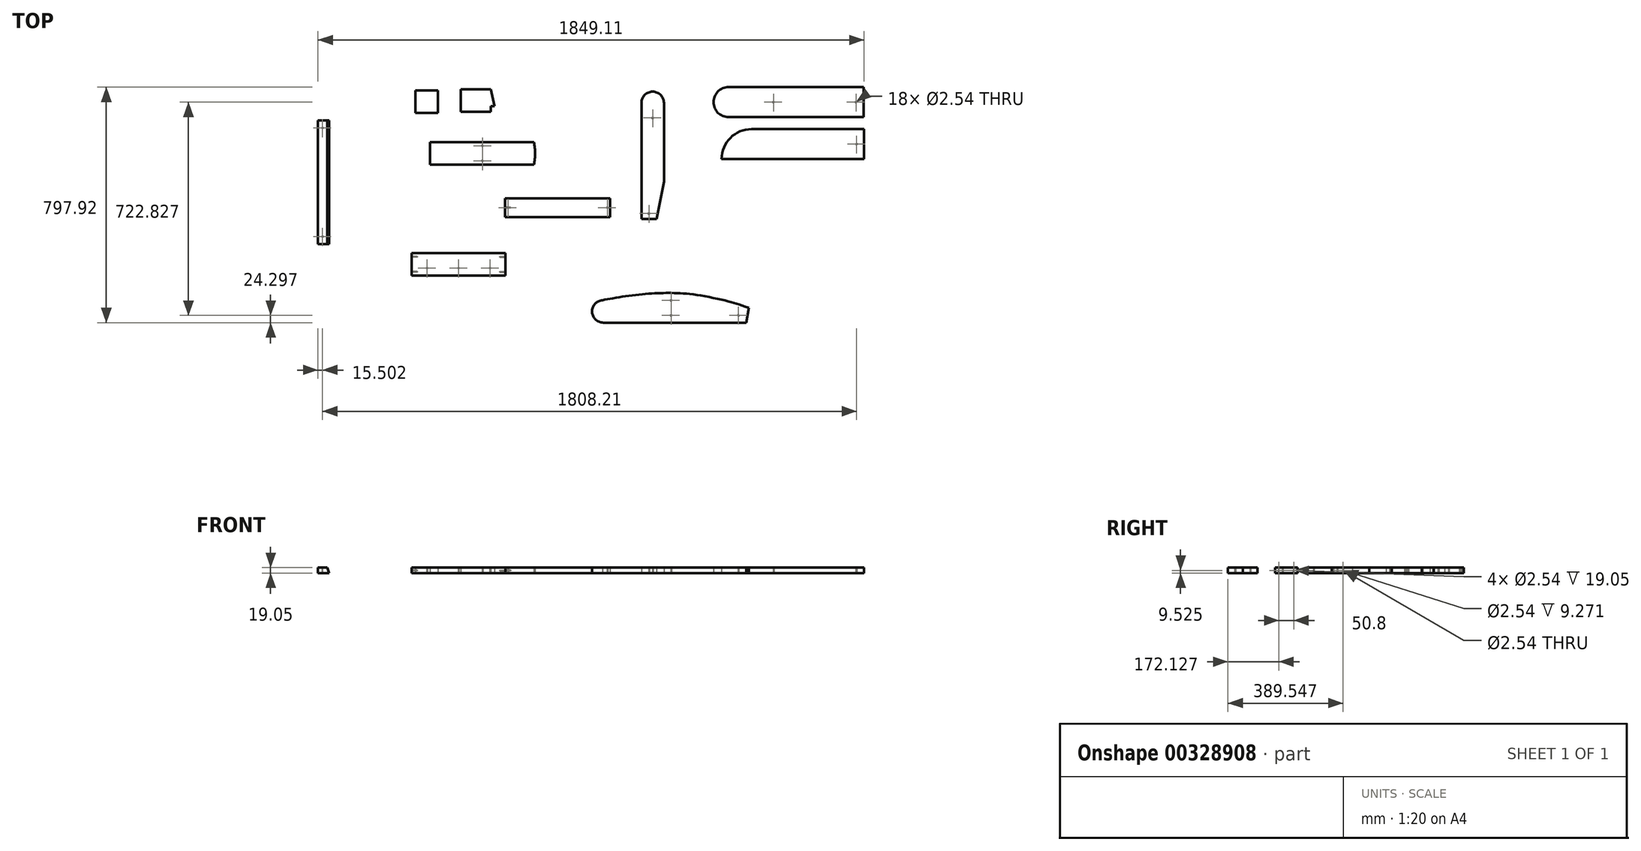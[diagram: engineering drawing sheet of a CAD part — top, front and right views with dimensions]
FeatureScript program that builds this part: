
annotation { "Feature Type Name" : "Feature", "Feature Type Description" : "" }
export const myFeature = defineFeature(function(context is Context, id is Id, definition is map)
    precondition{}
    {
        {
            var Q0;
            Q0=qCreatedBy(makeId("Top.planeOp"),FACE);
            var sketch = newSketch(context, id + "F0", { "sketchPlane" : qUnion([Q0])});
            skLineSegment(sketch, "E0", {"start": v(-60.93, -334.39) * mm, "end": v(-10.13, -334.39) * mm});
            skLineSegment(sketch, "E1", {"start": v(-10.13, -334.39) * mm, "end": v(15.27, -207.39) * mm});
            skLineSegment(sketch, "E2", {"start": v(15.27, -207.39) * mm, "end": v(15.27, 59.31) * mm});
            skLineSegment(sketch, "E3", {"start": v(-60.93, -334.39) * mm, "end": v(-60.93, 59.31) * mm});
            skLineSegment(sketch, "E4", {"start": v(-22.83, 97.41) * mm, "end": v(-22.83, 97.41) * mm});
            skPoint(sketch, "E5.visualSharp", {"position": v(-60.93, 97.41) * mm});
            skArc(sketch, "E5.filletArc", {"start": v(-22.83, 97.41) * mm, "mid": v(-49.77, 86.25) * mm, "end": v(-60.93, 59.31) * mm});
            skPoint(sketch, "E6.visualSharp", {"position": v(15.27, 97.41) * mm});
            skArc(sketch, "E6.filletArc", {"start": v(15.27, 59.31) * mm, "mid": v(4.1, 86.25) * mm, "end": v(-22.83, 97.41) * mm});
            skCircle(sketch, "E7", {"center": v(-35.53, -315.34) * mm, "radius": 1.27 * mm});
            skLineSegment(sketch, "E8", {"start": v(-22.83, 59.31) * mm, "end": v(-22.83, 8.51) * mm});
            skCircle(sketch, "E9", {"center": v(-22.83, 8.51) * mm, "radius": 1.27 * mm});
            skSolve(sketch);
        }
        {
            var Q0;
            Q0=makeQuery(id+"F0.imprint","IMPRINT",FACE,{"disambiguationData":[TD([[makeQuery(id+"F0.imprint","IMPRINT",EDGE,{"derivedFrom":sQuery(id+"F0.wireOp",EDGE,"E0")}),1.0]])]});
            extrude(context, id + "F1", {"entities" : qUnion([Q0]), "depth" : 19.05 * mm});
        }
        {
            var Q0;
            Q0=makeQuery(id+"F1.opExtrude","SWEPT_BODY",BODY,{"disambiguationData":[OSD([sQuery(id+"F0.wireOp",EDGE,"E0"),sQuery(id+"F0.wireOp",EDGE,"E1"),sQuery(id+"F0.wireOp",EDGE,"E2"),sQuery(id+"F0.wireOp",EDGE,"E3"),sQuery(id+"F0.wireOp",EDGE,"E5.filletArc"),sQuery(id+"F0.wireOp",EDGE,"E6.filletArc")])]});
            transform(context, id + "F2", {"entities" : qUnion([Q0]), "transformType" : TransformType.TRANSLATION_3D, "dx" : 812.8 * mm, "dy" : 0 * mm, "dz" : 0 * mm, "makeCopy" : true});
        }
        {
            var Q0;
            Q0=makeQuery(id+"F2.opPattern","COPY",BODY,{"derivedFrom":makeQuery(id+"F1.opExtrude","SWEPT_BODY",BODY,{"disambiguationData":[OSD([sQuery(id+"F0.wireOp",EDGE,"E0"),sQuery(id+"F0.wireOp",EDGE,"E1"),sQuery(id+"F0.wireOp",EDGE,"E2"),sQuery(id+"F0.wireOp",EDGE,"E3"),sQuery(id+"F0.wireOp",EDGE,"E5.filletArc"),sQuery(id+"F0.wireOp",EDGE,"E6.filletArc")])]}),"instanceName":"1"});
            deleteBodies(context, id + "F3", {"entities" : qUnion([Q0])});
        }
        {
            var Q0;
            Q0=qCreatedBy(makeId("Top.planeOp"),FACE);
            var sketch = newSketch(context, id + "F4", { "sketchPlane" : qUnion([Q0])});
            skLineSegment(sketch, "E10", {"start": v(693.1, -131) * mm, "end": v(210.5, -131) * mm});
            skLineSegment(sketch, "E11", {"start": v(210.5, -131) * mm, "end": v(210.5, -131) * mm});
            skLineSegment(sketch, "E12", {"start": v(312.1, -29.4) * mm, "end": v(693.1, -29.4) * mm});
            skLineSegment(sketch, "E13", {"start": v(693.1, -29.4) * mm, "end": v(693.1, -131) * mm});
            skPoint(sketch, "E14.visualSharp", {"position": v(210.5, -29.4) * mm});
            skArc(sketch, "E14.filletArc", {"start": v(312.1, -29.4) * mm, "mid": v(240.26, -59.17) * mm, "end": v(210.5, -131) * mm});
            skLineSegment(sketch, "E15", {"start": v(693.1, -80.2) * mm, "end": v(667.7, -80.2) * mm});
            skCircle(sketch, "E16", {"center": v(667.7, -80.2) * mm, "radius": 1.27 * mm});
            skSolve(sketch);
        }
        {
            var Q0;
            Q0=makeQuery(id+"F4.imprint","IMPRINT",FACE,{"disambiguationData":[TD([[makeQuery(id+"F4.imprint","IMPRINT",EDGE,{"derivedFrom":sQuery(id+"F4.wireOp",EDGE,"E10")}),-1.0]])]});
            extrude(context, id + "F5", {"entities" : qUnion([Q0]), "depth" : 19.05 * mm});
        }
        {
            var Q0;
            Q0=qCreatedBy(makeId("Top.planeOp"),FACE);
            var sketch = newSketch(context, id + "F6", { "sketchPlane" : qUnion([Q0])});
            skLineSegment(sketch, "E17", {"start": v(691.12, 11.16) * mm, "end": v(691.12, 112.76) * mm});
            skPoint(sketch, "E18.visualSharp", {"position": v(183.12, 112.76) * mm});
            skLineSegment(sketch, "E19", {"start": v(691.12, 61.96) * mm, "end": v(665.72, 61.96) * mm});
            skPoint(sketch, "E19.endSnap0", {"position": v(691.12, 61.96) * mm});
            skCircle(sketch, "E20", {"center": v(665.72, 61.96) * mm, "radius": 1.27 * mm});
            skCircle(sketch, "E21", {"center": v(386.32, 61.96) * mm, "radius": 1.27 * mm});
            skCircle(sketch, "E22", {"center": v(233.92, 61.96) * mm, "radius": 50.8 * mm});
            skPoint(sketch, "E22.centerSnap0", {"position": v(678.42, 61.96) * mm});
            skLineSegment(sketch, "E23", {"start": v(691.12, 112.76) * mm, "end": v(233.92, 112.76) * mm});
            skLineSegment(sketch, "E24", {"start": v(233.92, 112.76) * mm, "end": v(233.92, 11.16) * mm});
            skLineSegment(sketch, "E25", {"start": v(233.92, 11.16) * mm, "end": v(691.12, 11.16) * mm});
            skSolve(sketch);
        }
        {
            var Q0;
            Q0=qSketchRegion(id+"F6",true);
            extrude(context, id + "F7", {"entities" : qUnion([Q0]), "depth" : 19.05 * mm});
        }
        {
            var Q0;
            Q0=qCreatedBy(makeId("Top.planeOp"),FACE);
            var sketch = newSketch(context, id + "F8", { "sketchPlane" : qUnion([Q0])});
            skLineSegment(sketch, "E26", {"start": v(-189.76, -685.16) * mm, "end": v(293.53, -685.16) * mm});
            skPoint(sketch, "E27.visualSharp", {"position": v(-227.17, -685.16) * mm});
            skLineSegment(sketch, "E28", {"start": v(302.65, -634.36) * mm, "end": v(293.53, -685.16) * mm});
            skArc(sketch, "E29", {"start": v(-192.66, -609.06) * mm, "mid": v(-228.06, -648.51) * mm, "end": v(-189.76, -685.16) * mm});
            skLineSegment(sketch, "E30", {"start": v(39.53, -686.26) * mm, "end": v(39.53, -584.66) * mm});
            skFitSpline(sketch, "E31", {"points": [v(302.87, -634.43) * mm, v(233.44, -612.87) * mm, v(116.11, -589.95) * mm, v(39.53, -584.66) * mm, v(-71.82, -590.25) * mm, v(-192.66, -609.06) * mm], "startDerivative": vector(-538.27, 166.6) * mm, "endDerivative": vector(-386.07, -76.56) * mm});
            skLineSegment(sketch, "E32", {"start": v(39.53, -686.26) * mm, "end": v(39.53, -660.86) * mm});
            skLineSegment(sketch, "E33", {"start": v(39.53, -584.66) * mm, "end": v(39.53, -610.06) * mm});
            skCircle(sketch, "E34", {"center": v(39.53, -610.06) * mm, "radius": 1.27 * mm});
            skCircle(sketch, "E35", {"center": v(39.53, -660.86) * mm, "radius": 1.27 * mm});
            skCircle(sketch, "E36", {"center": v(267.44, -659.76) * mm, "radius": 1.27 * mm});
            skSolve(sketch);
        }
        {
            var Q0;
            {var subQ0=sQuery(id+"F8.wireOp",EDGE,"E29");Q0=makeQuery(id+"F8.imprint","IMPRINT",FACE,{"disambiguationData":[TD([[makeQuery(id+"F8.imprint","IMPRINT",EDGE,{"derivedFrom":subQ0}),1.0]])]});}
            var Q1;
            {var subQ0=sQuery(id+"F8.wireOp",EDGE,"E28");Q1=makeQuery(id+"F8.imprint","IMPRINT",FACE,{"disambiguationData":[TD([[makeQuery(id+"F8.imprint","IMPRINT",EDGE,{"derivedFrom":subQ0}),-1.0]])]});}
            extrude(context, id + "F9", {"entities" : qUnion([Q0, Q1]), "depth" : 19.05 * mm});
        }
        {
            var Q0;
            Q0=qCreatedBy(makeId("Top.planeOp"),FACE);
            var sketch = newSketch(context, id + "F10", { "sketchPlane" : qUnion([Q0])});
            skLineSegment(sketch, "E37", {"start": v(-838.56, -525.73) * mm, "end": v(-521.06, -525.73) * mm});
            skLineSegment(sketch, "E38", {"start": v(-521.06, -525.73) * mm, "end": v(-521.06, -449.53) * mm});
            skLineSegment(sketch, "E39", {"start": v(-838.56, -525.73) * mm, "end": v(-838.56, -449.53) * mm});
            skLineSegment(sketch, "E40", {"start": v(-838.56, -449.53) * mm, "end": v(-521.06, -449.53) * mm});
            skLineSegment(sketch, "E41", {"start": v(-838.56, -525.73) * mm, "end": v(-838.56, -500.33) * mm});
            skCircle(sketch, "E42", {"center": v(-786.55, -500.33) * mm, "radius": 1.27 * mm});
            skCircle(sketch, "E43", {"center": v(-679.87, -500.33) * mm, "radius": 1.27 * mm});
            skCircle(sketch, "E44", {"center": v(-573.19, -500.33) * mm, "radius": 1.27 * mm});
            skLineSegment(sketch, "E45", {"start": v(-679.81, -525.73) * mm, "end": v(-679.81, -478.75) * mm});
            skLineSegment(sketch, "E46", {"start": v(-679.81, -500.33) * mm, "end": v(-699.4, -500.33) * mm});
            skSolve(sketch);
        }
        {
            var Q0;
            Q0=makeQuery(id+"F10.imprint","IMPRINT",FACE,{"disambiguationData":[TD([[makeQuery(id+"F10.imprint","IMPRINT",EDGE,{"derivedFrom":sQuery(id+"F10.wireOp",EDGE,"E37")}),1.0]])]});
            extrude(context, id + "F11", {"entities" : qUnion([Q0]), "depth" : 19.05 * mm});
        }
        {
            var Q0;
            Q0=qCreatedBy(makeId("Front.planeOp"),FACE);
            var sketch = newSketch(context, id + "F12", { "sketchPlane" : qUnion([Q0])});
            skLineSegment(sketch, "E47", {"start": v(-1156, 0) * mm, "end": v(-1156, 19.05) * mm});
            skLineSegment(sketch, "E48", {"start": v(-1156, 0) * mm, "end": v(-1117.9, 0) * mm});
            skLineSegment(sketch, "E49", {"start": v(-1117.9, 0) * mm, "end": v(-1125, 19.05) * mm});
            skLineSegment(sketch, "E50", {"start": v(-1125, 19.05) * mm, "end": v(-1156, 19.05) * mm});
            skSolve(sketch);
        }
        {
            var Q0;
            Q0=makeQuery(id+"F12.imprint","IMPRINT",FACE,{"disambiguationData":[TD([[makeQuery(id+"F12.imprint","IMPRINT",EDGE,{"derivedFrom":sQuery(id+"F12.wireOp",EDGE,"E47")}),-1.0]])]});
            extrude(context, id + "F13", {"entities" : qUnion([Q0]), "depth" : 419.1 * mm});
        }
        {
            var Q0;
            Q0=qCreatedBy(makeId("Top.planeOp"),FACE);
            var sketch = newSketch(context, id + "F14", { "sketchPlane" : qUnion([Q0])});
            skLineSegment(sketch, "E51", {"start": v(-522.58, -327.36) * mm, "end": v(-166.98, -327.36) * mm});
            skLineSegment(sketch, "E52", {"start": v(-166.98, -327.36) * mm, "end": v(-166.98, -263.86) * mm});
            skLineSegment(sketch, "E53", {"start": v(-166.98, -263.86) * mm, "end": v(-522.58, -263.86) * mm});
            skLineSegment(sketch, "E54", {"start": v(-522.58, -263.86) * mm, "end": v(-522.58, -327.36) * mm});
            skCircle(sketch, "E55", {"center": v(-512.8, -295.61) * mm, "radius": 1.27 * mm});
            skPoint(sketch, "E55.centerSnap0", {"position": v(-522.58, -295.61) * mm});
            skLineSegment(sketch, "E56", {"start": v(-166.98, -295.61) * mm, "end": v(-176.26, -295.61) * mm});
            skCircle(sketch, "E57", {"center": v(-176.26, -295.61) * mm, "radius": 1.27 * mm});
            skSolve(sketch);
        }
        {
            var Q0;
            Q0=makeQuery(id+"F14.imprint","IMPRINT",FACE,{"disambiguationData":[TD([[makeQuery(id+"F14.imprint","IMPRINT",EDGE,{"derivedFrom":sQuery(id+"F14.wireOp",EDGE,"E51")}),1.0]])]});
            extrude(context, id + "F15", {"entities" : qUnion([Q0]), "depth" : 19.05 * mm});
        }
        {
            var Q0;
            Q0=qCreatedBy(makeId("Top.planeOp"),FACE);
            var sketch = newSketch(context, id + "F16", { "sketchPlane" : qUnion([Q0])});
            skLineSegment(sketch, "E58", {"start": v(-776.42, -73.8) * mm, "end": v(-776.42, -150) * mm});
            skLineSegment(sketch, "E59", {"start": v(-776.42, -150) * mm, "end": v(-424.95, -150) * mm});
            skLineSegment(sketch, "E60", {"start": v(-424.95, -73.8) * mm, "end": v(-776.42, -73.8) * mm});
            skLineSegment(sketch, "E61", {"start": v(-598.62, -150) * mm, "end": v(-598.62, -137.3) * mm});
            skPoint(sketch, "E62.endSnap0", {"position": v(-598.62, -73.8) * mm});
            skCircle(sketch, "E63", {"center": v(-598.62, -86.5) * mm, "radius": 1.27 * mm});
            skCircle(sketch, "E64", {"center": v(-598.62, -137.3) * mm, "radius": 1.27 * mm});
            skPoint(sketch, "E65.centerSnap0", {"position": v(-776.42, -111.9) * mm});
            skArc(sketch, "E66.trimOffspring", {"start": v(-424.95, -150) * mm, "mid": v(-420.82, -111.9) * mm, "end": v(-424.95, -73.8) * mm});
            skPoint(sketch, "E67.orphan", {"position": v(-420.82, -73.8) * mm});
            skPoint(sketch, "E68.orphan", {"position": v(-420.82, -150) * mm});
            skSolve(sketch);
        }
        {
            var Q0;
            Q0=makeQuery(id+"F16.imprint","IMPRINT",FACE,{"disambiguationData":[TD([[makeQuery(id+"F16.imprint","IMPRINT",EDGE,{"derivedFrom":sQuery(id+"F16.wireOp",EDGE,"E58")}),1.0]])]});
            extrude(context, id + "F17", {"entities" : qUnion([Q0]), "depth" : 19.05 * mm});
        }
        {
            var Q0;
            Q0=qCreatedBy(makeId("Top.planeOp"),FACE);
            var sketch = newSketch(context, id + "F18", { "sketchPlane" : qUnion([Q0])});
            skLineSegment(sketch, "E69", {"start": v(-750.24, 101.28) * mm, "end": v(-750.24, 25.08) * mm});
            skLineSegment(sketch, "E70", {"start": v(-750.24, 25.08) * mm, "end": v(-826.44, 25.08) * mm});
            skLineSegment(sketch, "E71", {"start": v(-826.44, 25.08) * mm, "end": v(-826.44, 101.28) * mm});
            skLineSegment(sketch, "E72", {"start": v(-826.44, 101.28) * mm, "end": v(-750.24, 101.28) * mm});
            skSolve(sketch);
        }
        {
            var Q0;
            Q0=makeQuery(id+"F18.imprint","IMPRINT",FACE,{"disambiguationData":[TD([[makeQuery(id+"F18.imprint","IMPRINT",EDGE,{"derivedFrom":sQuery(id+"F18.wireOp",EDGE,"E69")}),-1.0]])]});
            extrude(context, id + "F19", {"entities" : qUnion([Q0]), "depth" : 19.05 * mm});
        }
        {
            var Q0;
            Q0=qCreatedBy(makeId("Top.planeOp"),FACE);
            var sketch = newSketch(context, id + "F20", { "sketchPlane" : qUnion([Q0])});
            skLineSegment(sketch, "E73", {"start": v(-671.98, 105.83) * mm, "end": v(-671.98, 29.63) * mm});
            skLineSegment(sketch, "E74", {"start": v(-671.98, 29.63) * mm, "end": v(-570.38, 29.63) * mm});
            skLineSegment(sketch, "E75", {"start": v(-570.38, 105.83) * mm, "end": v(-671.98, 105.83) * mm});
            skLineSegment(sketch, "E76", {"start": v(-570.38, 29.63) * mm, "end": v(-570.38, 48.68) * mm});
            skLineSegment(sketch, "E77", {"start": v(-570.38, 48.68) * mm, "end": v(-557.68, 48.68) * mm});
            skLineSegment(sketch, "E78", {"start": v(-557.68, 48.68) * mm, "end": v(-570.38, 105.83) * mm});
            skSolve(sketch);
        }
        {
            var Q0;
            Q0=makeQuery(id+"F20.imprint","IMPRINT",FACE,{"disambiguationData":[TD([[makeQuery(id+"F20.imprint","IMPRINT",EDGE,{"derivedFrom":sQuery(id+"F20.wireOp",EDGE,"E73")}),1.0]])]});
            extrude(context, id + "F21", {"entities" : qUnion([Q0]), "depth" : 19.05 * mm});
        }
        {
            var Q0;
            Q0=sQuery(id+"F0.wireOp",EDGE,"E7");
            extrude(context, id + "F22", {"bodyType" : ToolBodyType.SURFACE, "surfaceEntities" : qUnion([Q0]), "depth" : 19.05 * mm});
        }
        {
            var Q0;
            Q0=sQuery(id+"F0.wireOp",EDGE,"E9");
            extrude(context, id + "F23", {"bodyType" : ToolBodyType.SURFACE, "surfaceEntities" : qUnion([Q0]), "depth" : 25.4 * mm});
        }
        {
            var Q0;
            Q0=sQuery(id+"F8.wireOp",EDGE,"E34");
            extrude(context, id + "F24", {"bodyType" : ToolBodyType.SURFACE, "surfaceEntities" : qUnion([Q0]), "depth" : 25.4 * mm});
        }
        {
            var Q0;
            Q0=makeQuery(id+"F13.opExtrude","SWEPT_FACE",FACE,{"disambiguationData":[OSD([sQuery(id+"F12.wireOp",EDGE,"E50")])]});
            var sketch = newSketch(context, id + "F25", { "sketchPlane" : qUnion([Q0])});
            skLineSegment(sketch, "E79", {"start": v(-1140.5, -419.1) * mm, "end": v(-1140.5, -393.7) * mm});
            skCircle(sketch, "E80", {"center": v(-1140.5, -393.7) * mm, "radius": 1.27 * mm});
            skLineSegment(sketch, "E81", {"start": v(-1140.5, 0) * mm, "end": v(-1140.5, -25.4) * mm});
            skCircle(sketch, "E82", {"center": v(-1140.5, -25.4) * mm, "radius": 1.27 * mm});
            skSolve(sketch);
        }
        {
            var Q0;
            Q0=qSketchRegion(id+"F25",true);
            extrude(context, id + "F26", {"entities" : qUnion([Q0]), "operationType" : NewBodyOperationType.REMOVE, "depth" : -19.05 * mm});
        }
        {
            var Q0;
            Q0=makeQuery(id+"F11.opExtrude","SWEPT_FACE",FACE,{"disambiguationData":[OSD([sQuery(id+"F10.wireOp",EDGE,"E39"),sQuery(id+"F10.wireOp",EDGE,"E41")])]});
            var sketch = newSketch(context, id + "F27", { "sketchPlane" : qUnion([Q0])});
            skLineSegment(sketch, "E83", {"start": v(525.73, 9.53) * mm, "end": v(513.03, 9.53) * mm});
            skCircle(sketch, "E84", {"center": v(462.23, 9.53) * mm, "radius": 1.27 * mm});
            skCircle(sketch, "E85", {"center": v(513.03, 9.53) * mm, "radius": 1.27 * mm});
            skSolve(sketch);
        }
        {
            var Q0;
            Q0=qSketchRegion(id+"F27",true);
            extrude(context, id + "F28", {"entities" : qUnion([Q0]), "operationType" : NewBodyOperationType.REMOVE, "oppositeDirection" : true, "depth" : 19.05 * mm});
        }
        {
            var Q0;
            Q0=makeQuery(id+"F11.opExtrude","SWEPT_FACE",FACE,{"disambiguationData":[OSD([sQuery(id+"F10.wireOp",EDGE,"E38")])]});
            var sketch = newSketch(context, id + "F29", { "sketchPlane" : qUnion([Q0])});
            skLineSegment(sketch, "E86", {"start": v(-525.73, 9.53) * mm, "end": v(-513.03, 9.53) * mm});
            skCircle(sketch, "E87", {"center": v(-462.23, 9.53) * mm, "radius": 1.27 * mm});
            skCircle(sketch, "E88", {"center": v(-513.03, 9.53) * mm, "radius": 1.27 * mm});
            skSolve(sketch);
        }
        {
            var Q0;
            Q0=qSketchRegion(id+"F29",true);
            extrude(context, id + "F30", {"entities" : qUnion([Q0]), "operationType" : NewBodyOperationType.REMOVE, "oppositeDirection" : true, "depth" : 19.05 * mm});
        }
        {
            var Q0;
            Q0=makeQuery(id+"F15.opExtrude","SWEPT_FACE",FACE,{"disambiguationData":[OSD([sQuery(id+"F14.wireOp",EDGE,"E54")])]});
            var sketch = newSketch(context, id + "F31", { "sketchPlane" : qUnion([Q0])});
            skCircle(sketch, "E89", {"center": v(295.61, 9.53) * mm, "radius": 1.27 * mm});
            skPoint(sketch, "E89.centerSnap0", {"position": v(295.61, 19.05) * mm});
            skPoint(sketch, "E89.centerSnap1", {"position": v(263.86, 9.53) * mm});
            skSolve(sketch);
        }
        {
            var Q0;
            Q0=qSketchRegion(id+"F31",true);
            extrude(context, id + "F32", {"entities" : qUnion([Q0]), "operationType" : NewBodyOperationType.REMOVE, "oppositeDirection" : true, "depth" : 19.05 * mm});
        }
    });
